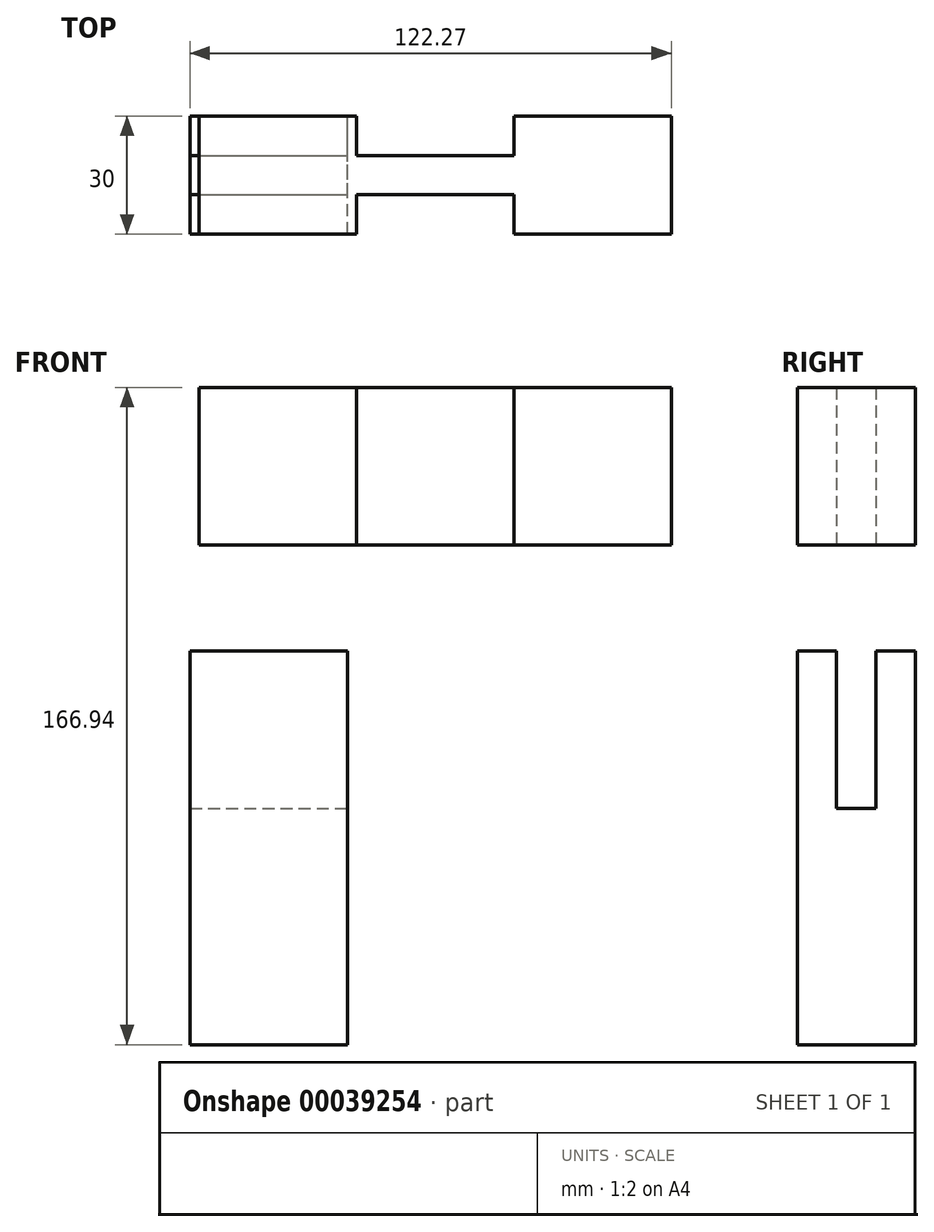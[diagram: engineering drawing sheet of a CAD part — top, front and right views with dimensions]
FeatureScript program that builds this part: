
annotation { "Feature Type Name" : "Feature", "Feature Type Description" : "" }
export const myFeature = defineFeature(function(context is Context, id is Id, definition is map)
    precondition{}
    {
        {
            var Q0;
            Q0=qCreatedBy(makeId("Front.planeOp"),FACE);
            var sketch = newSketch(context, id + "F0", { "sketchPlane" : qUnion([Q0])});
            skLineSegment(sketch, "E0.bottom", {"start": v(-59.26, 52.39) * mm, "end": v(-19.26, 52.39) * mm});
            skLineSegment(sketch, "E0.top", {"start": v(-59.26, -47.61) * mm, "end": v(-19.26, -47.61) * mm});
            skLineSegment(sketch, "E0.left", {"start": v(-59.26, 52.39) * mm, "end": v(-59.26, -47.61) * mm});
            skLineSegment(sketch, "E0.right", {"start": v(-19.26, 52.39) * mm, "end": v(-19.26, -47.61) * mm});
            skSolve(sketch);
        }
        {
            var Q0;
            Q0=makeQuery(id+"F0.imprint","IMPRINT",FACE,{"disambiguationData":[TD([[makeQuery(id+"F0.imprint","IMPRINT",EDGE,{"derivedFrom":sQuery(id+"F0.wireOp",EDGE,"E0.bottom")}),-1.0]])]});
            extrude(context, id + "F1", {"entities" : qUnion([Q0]), "depth" : 30 * mm});
        }
        {
            var Q0;
            Q0=makeQuery(id+"F1.opExtrude","SWEPT_FACE",FACE,{"disambiguationData":[OSD([sQuery(id+"F0.wireOp",EDGE,"E0.bottom")])]});
            var sketch = newSketch(context, id + "F2", { "sketchPlane" : qUnion([Q0])});
            skLineSegment(sketch, "E1.bottom", {"start": v(-59.26, -10) * mm, "end": v(-19.26, -10) * mm});
            skLineSegment(sketch, "E1.top", {"start": v(-59.26, -20) * mm, "end": v(-19.26, -20) * mm});
            skLineSegment(sketch, "E1.left", {"start": v(-59.26, -10) * mm, "end": v(-59.26, -20) * mm});
            skLineSegment(sketch, "E1.right", {"start": v(-19.26, -10) * mm, "end": v(-19.26, -20) * mm});
            skSolve(sketch);
        }
        {
            var Q0;
            Q0=makeQuery(id+"F2.imprint","IMPRINT",FACE,{"disambiguationData":[TD([[makeQuery(id+"F2.imprint","IMPRINT",EDGE,{"derivedFrom":sQuery(id+"F2.wireOp",EDGE,"E1.bottom")}),-1.0]])]});
            extrude(context, id + "F3", {"entities" : qUnion([Q0]), "operationType" : NewBodyOperationType.REMOVE, "oppositeDirection" : true, "depth" : 40 * mm});
        }
        {
            var Q0;
            Q0=qCreatedBy(makeId("Front.planeOp"),FACE);
            var sketch = newSketch(context, id + "F4", { "sketchPlane" : qUnion([Q0])});
            skLineSegment(sketch, "E2.bottom", {"start": v(-56.99, 119.33) * mm, "end": v(63.01, 119.33) * mm});
            skLineSegment(sketch, "E2.top", {"start": v(-56.99, 79.33) * mm, "end": v(63.01, 79.33) * mm});
            skLineSegment(sketch, "E2.left", {"start": v(-56.99, 119.33) * mm, "end": v(-56.99, 79.33) * mm});
            skLineSegment(sketch, "E2.right", {"start": v(63.01, 119.33) * mm, "end": v(63.01, 79.33) * mm});
            skSolve(sketch);
        }
        {
            var Q0;
            Q0=makeQuery(id+"F4.imprint","IMPRINT",FACE,{"disambiguationData":[TD([[makeQuery(id+"F4.imprint","IMPRINT",EDGE,{"derivedFrom":sQuery(id+"F4.wireOp",EDGE,"E2.bottom")}),-1.0]])]});
            extrude(context, id + "F5", {"entities" : qUnion([Q0]), "depth" : 30 * mm});
        }
        {
            var Q0;
            Q0=makeQuery(id+"F5.opExtrude","CAP_FACE",FACE,{"disambiguationData":[OSD([sQuery(id+"F4.wireOp",EDGE,"E2.bottom"),sQuery(id+"F4.wireOp",EDGE,"E2.top"),sQuery(id+"F4.wireOp",EDGE,"E2.left"),sQuery(id+"F4.wireOp",EDGE,"E2.right")])],"isStart":false});
            var sketch = newSketch(context, id + "F6", { "sketchPlane" : qUnion([Q0])});
            skLineSegment(sketch, "E3.bottom", {"start": v(-16.99, 119.33) * mm, "end": v(23.01, 119.33) * mm});
            skLineSegment(sketch, "E3.top", {"start": v(-16.99, 79.33) * mm, "end": v(23.01, 79.33) * mm});
            skLineSegment(sketch, "E3.left", {"start": v(-16.99, 119.33) * mm, "end": v(-16.99, 79.33) * mm});
            skLineSegment(sketch, "E3.right", {"start": v(23.01, 119.33) * mm, "end": v(23.01, 79.33) * mm});
            skSolve(sketch);
        }
        {
            var Q0;
            Q0=makeQuery(id+"F6.imprint","IMPRINT",FACE,{"disambiguationData":[TD([[makeQuery(id+"F6.imprint","IMPRINT",EDGE,{"derivedFrom":sQuery(id+"F6.wireOp",EDGE,"E3.bottom")}),-1.0]])]});
            extrude(context, id + "F7", {"entities" : qUnion([Q0]), "operationType" : NewBodyOperationType.REMOVE, "oppositeDirection" : true, "depth" : 10 * mm});
        }
        {
            var Q0;
            Q0=makeQuery(id+"F5.opExtrude","CAP_FACE",FACE,{"disambiguationData":[OSD([sQuery(id+"F4.wireOp",EDGE,"E2.bottom"),sQuery(id+"F4.wireOp",EDGE,"E2.top"),sQuery(id+"F4.wireOp",EDGE,"E2.left"),sQuery(id+"F4.wireOp",EDGE,"E2.right")])],"isStart":true});
            var sketch = newSketch(context, id + "F8", { "sketchPlane" : qUnion([Q0])});
            skLineSegment(sketch, "E4.bottom", {"start": v(-23.01, 119.33) * mm, "end": v(16.99, 119.33) * mm});
            skLineSegment(sketch, "E4.top", {"start": v(-23.01, 79.33) * mm, "end": v(16.99, 79.33) * mm});
            skLineSegment(sketch, "E4.left", {"start": v(-23.01, 119.33) * mm, "end": v(-23.01, 79.33) * mm});
            skLineSegment(sketch, "E4.right", {"start": v(16.99, 119.33) * mm, "end": v(16.99, 79.33) * mm});
            skSolve(sketch);
        }
        {
            var Q0;
            Q0=makeQuery(id+"F8.imprint","IMPRINT",FACE,{"disambiguationData":[TD([[makeQuery(id+"F8.imprint","IMPRINT",EDGE,{"derivedFrom":sQuery(id+"F8.wireOp",EDGE,"E4.bottom")}),1.0]])]});
            extrude(context, id + "F9", {"entities" : qUnion([Q0]), "operationType" : NewBodyOperationType.REMOVE, "oppositeDirection" : true, "depth" : 10 * mm});
        }
    });
